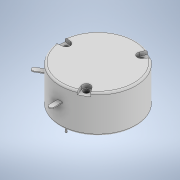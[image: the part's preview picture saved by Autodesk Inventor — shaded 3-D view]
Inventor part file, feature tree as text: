
AUTODESK INVENTOR PART (.ipt)
format: ipt  version: 2021 (Build 250183000, 183)  size: 252,416 bytes
history: native  units: mm
features: projected_geometry x7, sketch x6, extrude x5, fillet x2, hole x1, plane x1
ambient origin geometry x8: Origin, YZ Plane, XZ Plane, XY Plane, X Axis, Y Axis, Z Axis, Center Point
bodies: Solid1 (feature_tree)
feature tree (22):
  extrude  "Extrusion1"  Depth=20.4mm TaperAngle=0.0deg
  hole  "Hole1"  [1 undecoded]
  extrude  "Extrusion2"  Depth=2.0mm TaperAngle=0.0deg
  plane  "Work Plane1"
  extrude  "Extrusion3"  TaperAngle=30.0deg  [1 undecoded]
  extrude  "Extrusion4"  TaperAngle=60.0deg  [1 undecoded]
  extrude  "Extrusion5"  Depth=6.0mm
  fillet  "Fillet1"  Radius=2.5mm
  fillet  "Fillet2"  Radius=2.5mm
  sketch  "Sketch1"  dims[d0=41.0mm d1=20.4mm d2=0.0mm]
  sketch  "Sketch2"  dims[d3=34.4mm d4=30.0mm d6=360.0deg]
  sketch  "Sketch3"  dims[d8=3.0mm d9=6.0mm d10=4.4mm d11=2.0mm d12=90.0deg d13=8.0mm d14=20.594885mm d15=2.0mm d16=0.0mm]
  projected_geometry  "Projected Loop1"
  sketch  "Sketch4"  dims[d17=-8.0mm d18=30.0deg]
  projected_geometry  "Projected Loop2"
  sketch  "Sketch5"  dims[d19=30.0deg d20=60.0deg]
  projected_geometry  "Projected Loop3"
  projected_geometry  "Projected Loop4"
  projected_geometry  "Projected Loop5"
  projected_geometry  "Projected Loop6"
  sketch  "Sketch7"  dims[d21=2.5mm d22=6.0mm d23=2.5mm d24=2.5mm d25=6.0mm d26=6.0mm d27=0.5mm d28=0.0mm d29=34.4mm d30=3.0mm d31=3.0mm d32=3.0mm d33=0.2mm d34=0.0mm d36=1.0mm d37=1.0mm d38=1.0mm d39=4.5mm d40=0.0mm d41=0.5mm d42=1.0mm]
  projected_geometry  "Projected Loop8"
note: 3 required parameter values undecoded (feature->parameter linkage not recoverable at this tier; creation-order binding heuristic only, values carry confidence <= 0.55)
